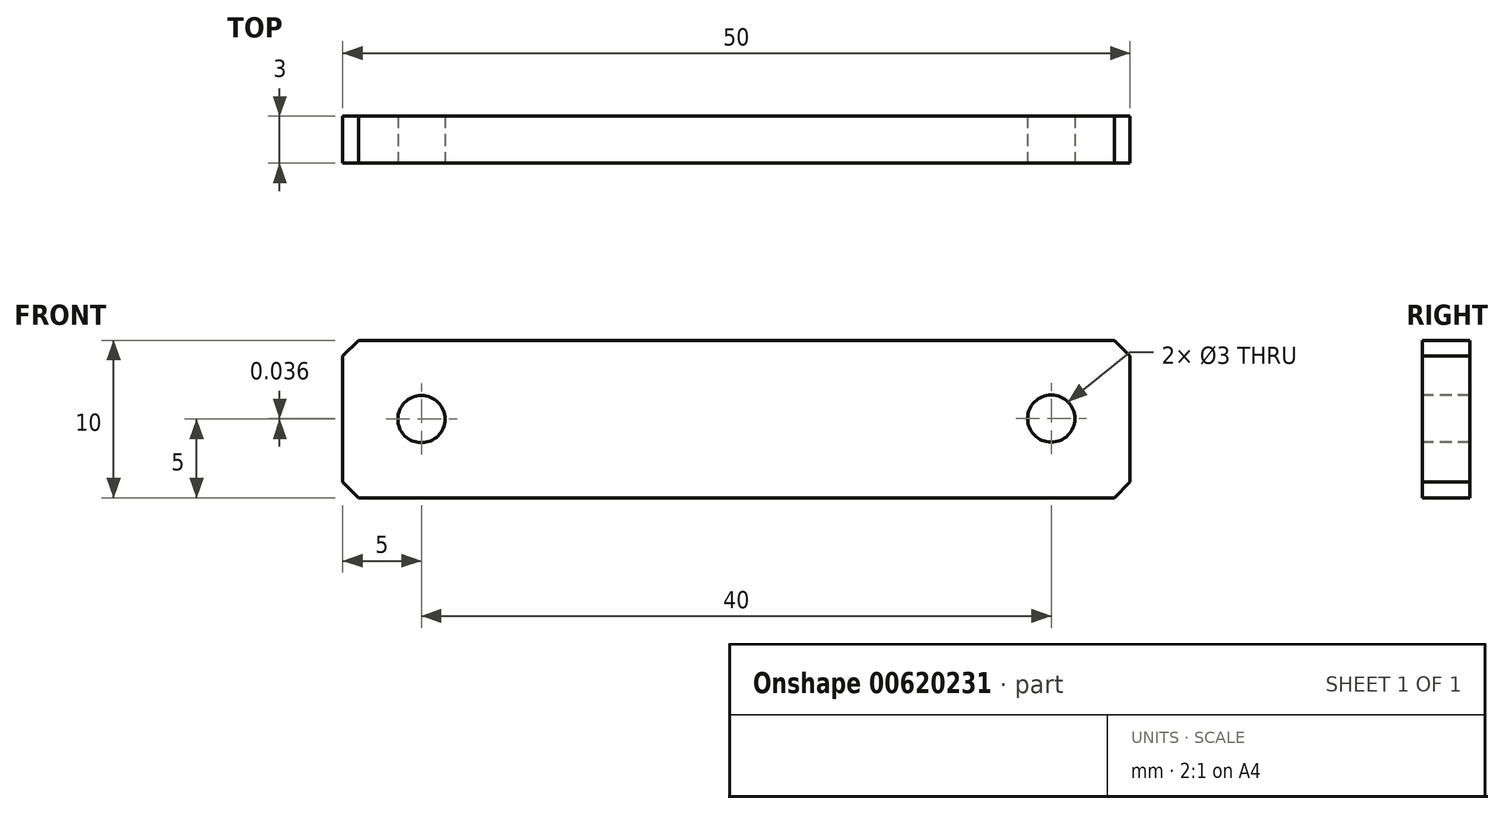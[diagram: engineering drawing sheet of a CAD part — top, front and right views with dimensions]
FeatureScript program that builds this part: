
annotation { "Feature Type Name" : "Feature", "Feature Type Description" : "" }
export const myFeature = defineFeature(function(context is Context, id is Id, definition is map)
    precondition{}
    {
        {
            var Q0;
            Q0=qCreatedBy(makeId("Front.planeOp"),FACE);
            var sketch = newSketch(context, id + "F0", { "sketchPlane" : qUnion([Q0])});
            skLineSegment(sketch, "E0.bottom", {"start": v(0, 0) * mm, "end": v(-50, 0) * mm});
            skLineSegment(sketch, "E0.top", {"start": v(0, 10) * mm, "end": v(-50, 10) * mm});
            skLineSegment(sketch, "E0.left", {"start": v(0, 0) * mm, "end": v(0, 10) * mm});
            skLineSegment(sketch, "E0.right", {"start": v(-50, 0) * mm, "end": v(-50, 10) * mm});
            skSolve(sketch);
        }
        {
            var Q0;
            Q0 = qSketchRegion(id + "F0", true);
            extrude(context, id + "F1", {"entities" : qUnion([Q0]), "depth" : 3 * mm, "offsetDistance" : 25 * mm});
        }
        {
            var Q0;
            Q0=makeQuery(id+"F1.opExtrude","CAP_FACE",FACE,{"disambiguationData":[OSD([sQuery(id+"F0.wireOp",EDGE,"E0.bottom"),sQuery(id+"F0.wireOp",EDGE,"E0.top"),sQuery(id+"F0.wireOp",EDGE,"E0.left"),sQuery(id+"F0.wireOp",EDGE,"E0.right")])],"isStart":false});
            var sketch = newSketch(context, id + "F2", { "sketchPlane" : qUnion([Q0])});
            skCircle(sketch, "E1", {"center": v(-45, 5) * mm, "radius": 1.5 * mm});
            skPoint(sketch, "E1.centerSnap0", {"position": v(-50, 5) * mm});
            skCircle(sketch, "E2", {"center": v(-5, 5.04) * mm, "radius": 1.5 * mm});
            skLineSegment(sketch, "E3", {"start": v(-25, 0) * mm, "end": v(-25, 2.16) * mm});
            skPoint(sketch, "E3.endSnap0", {"position": v(-25, 0) * mm});
            skSolve(sketch);
        }
        {
            var Q0;
            Q0 = qSketchRegion(id + "F2", true);
            extrude(context, id + "F3", {"entities" : qUnion([Q0]), "operationType" : NewBodyOperationType.REMOVE, "oppositeDirection" : true, "depth" : 5 * mm, "offsetDistance" : 25 * mm});
        }
        {
            var Q0;
            Q0=makeQuery(id+"F1.opExtrude","SWEPT_EDGE",EDGE,{"disambiguationData":[OSD([sQuery(id+"F0.wireOp",EDGE,"E0.top"),sQuery(id+"F0.wireOp",EDGE,"E0.left")])]});
            var Q1;
            Q1=makeQuery(id+"F1.opExtrude","SWEPT_EDGE",EDGE,{"disambiguationData":[OSD([sQuery(id+"F0.wireOp",EDGE,"E0.bottom"),sQuery(id+"F0.wireOp",EDGE,"E0.left")])]});
            var Q2;
            Q2=makeQuery(id+"F1.opExtrude","SWEPT_EDGE",EDGE,{"disambiguationData":[OSD([sQuery(id+"F0.wireOp",EDGE,"E0.top"),sQuery(id+"F0.wireOp",EDGE,"E0.right")])]});
            var Q3;
            Q3=makeQuery(id+"F1.opExtrude","SWEPT_EDGE",EDGE,{"disambiguationData":[OSD([sQuery(id+"F0.wireOp",EDGE,"E0.bottom"),sQuery(id+"F0.wireOp",EDGE,"E0.right")])]});
            chamfer(context, id + "F4", {"entities" : qUnion([Q0, Q1, Q2, Q3]), "width" : 1 * mm, "tangentPropagation" : true});
        }
    });
